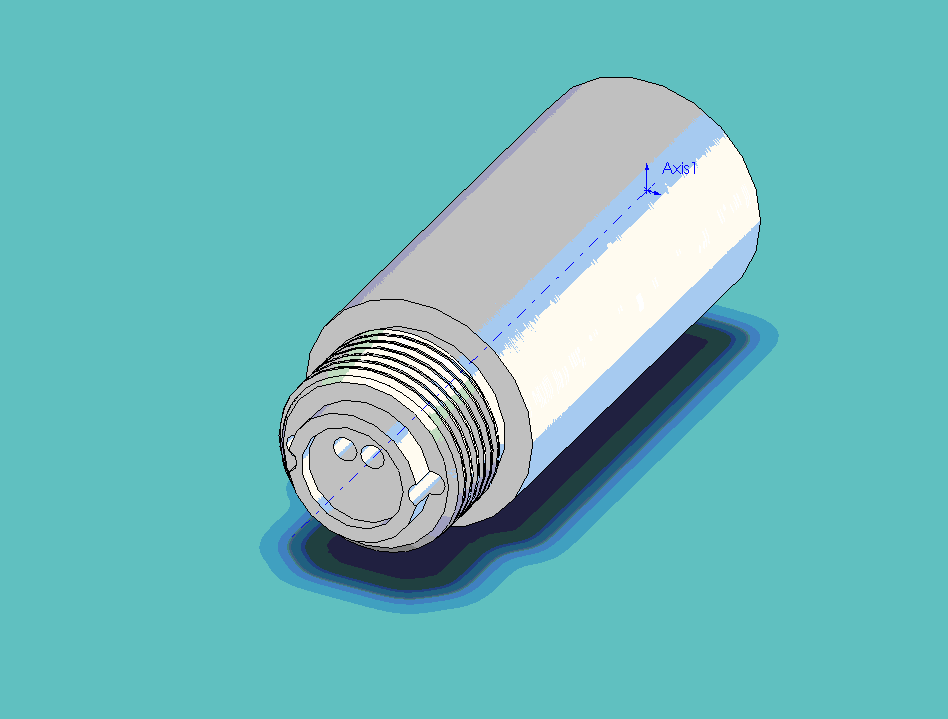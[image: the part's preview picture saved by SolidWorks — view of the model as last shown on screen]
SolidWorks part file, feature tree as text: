
SOLIDWORKS PART (.sldprt)
format: sldprt  version: not decoded by parser v0  size: 745,984 bytes
history: native  units: mm
features: sketch x10, extrude x3, cut_extrude x3, cut_revolve x2, material x1, helix x1, sweep x1 (+14 scaffold rows collapsed)
feature tree (35):
  scaffold x14  (default folders/planes/origin — collapsed)
  material  "6061-T6"
  sketch  "Sketch1"  dims[D1=22.86mm]
  extrude  "Body"  Depth=43.45mm
  sketch  "Sketch2"  dims[D1=19.05mm]
  extrude  "Extrude2"  Depth=10.16mm
  sketch  "Sketch3"  dims[D1=13.0mm]
  extrude  "0.512""  Depth=2.54mm
  sketch  "Sketch4"  dims[D1=8.675mm D2=1.53mm]
  cut_revolve  "0.683" #017 O-Ring Groove"  Angle=360deg
  sketch  "Sketch5"  dims[D1=18.542mm]
  helix  "Helix/Spiral1"  Pitch=12.5mm
  sketch  "Sketch7"  dims[c1.D1=1.27mm c1.D2=0.3175mm c1.D3=~0.15875mm c1.D4=8.9408mm c1.D5=9.5885mm c2.D1=~1.099852mm c3.D1=60.0deg c3.D2=1.27mm c3.D3=0.3175mm c3.D4=~0.15875mm c3.D6=9.525mm]
  sweep  "Male 3/4-20" Threads"
  sketch  "Sketch8"  dims[D1=0.5mm D2=1.2mm D3=9.525mm]
  cut_revolve  "Break Sharp Edges"  Angle=360deg
  sketch  "Sketch9"  dims[D1=~11.113328mm]
  cut_extrude  "HPA #010 O-Ring Housing"  Depth=1.2192mm
  sketch  "Sketch10"  dims[c1.D1=~2.38125mm c1.D2=1.1mm c1.D3=~2.38125mm c2.D2=~2.38125mm c2.D4=2.75mm]
  cut_extrude  "HPA Intake (dual 3/32")"  Depth=10mm
  sketch  "Sketch11"  dims[c1.D1=~1.710031mm c1.D2=~2.38125mm c1.D3=~2.38125mm c2.D1=0.5mm c2.D2=~1.108209mm c2.D3=0.5mm]
  cut_extrude  "LPA Exhaust"  Depth=10mm
decode coverage: 19 of 20 modeling features carry decoded parameters
note: ~ marks probable driven/reference dimensions
note: suppression state not decoded; provenance and decode notes live in map.json
